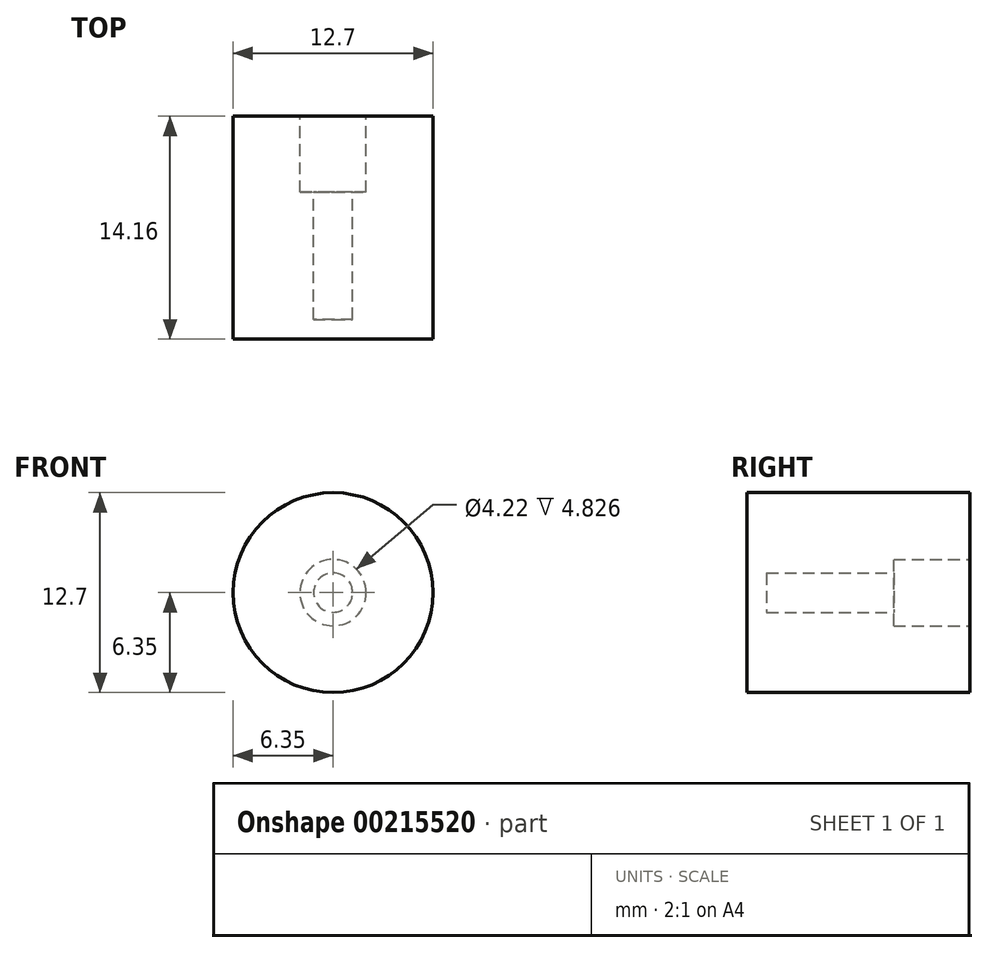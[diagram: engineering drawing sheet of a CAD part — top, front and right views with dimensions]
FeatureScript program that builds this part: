
annotation { "Feature Type Name" : "Feature", "Feature Type Description" : "" }
export const myFeature = defineFeature(function(context is Context, id is Id, definition is map)
    precondition{}
    {
        {
            var Q0;
            Q0=qCreatedBy(makeId("Front.planeOp"),FACE);
            var sketch = newSketch(context, id + "F0", { "sketchPlane" : qUnion([Q0])});
            skCircle(sketch, "E0", {"center": v(0, 0) * mm, "radius": 2.1 * mm});
            skCircle(sketch, "E1", {"center": v(0, 0) * mm, "radius": 6.35 * mm});
            skSolve(sketch);
        }
        {
            var Q0;
            Q0=makeQuery(id+"F0.imprint","IMPRINT",FACE,{"disambiguationData":[TD([[makeQuery(id+"F0.imprint","IMPRINT",EDGE,{"derivedFrom":sQuery(id+"F0.wireOp",EDGE,"E0")}),-1.0]])]});
            extrude(context, id + "F1", {"entities" : qUnion([Q0]), "depth" : 4.83 * mm});
        }
        {
            var Q0;
            Q0=makeQuery(id+"F1.opExtrude","CAP_FACE",FACE,{"disambiguationData":[OSD([sQuery(id+"F0.wireOp",EDGE,"E0"),sQuery(id+"F0.wireOp",EDGE,"E1")])],"isStart":false});
            var sketch = newSketch(context, id + "F2", { "sketchPlane" : qUnion([Q0])});
            skCircle(sketch, "E2", {"center": v(0, 0) * mm, "radius": 6.35 * mm});
            skSolve(sketch);
        }
        {
            var Q0;
            Q0=qSketchRegion(id+"F2",true);
            extrude(context, id + "F3", {"entities" : qUnion([Q0]), "operationType" : NewBodyOperationType.ADD, "depth" : 9.33 * mm});
        }
        {
            var Q0;
            Q0=makeQuery(id+"F3.opExtrude","CAP_FACE",FACE,{"disambiguationData":[OSD([sQuery(id+"F2.wireOp",EDGE,"E2")])],"isStart":true});
            var sketch = newSketch(context, id + "F4", { "sketchPlane" : qUnion([Q0])});
            skCircle(sketch, "E3", {"center": v(0, 0) * mm, "radius": 1.24 * mm});
            skSolve(sketch);
        }
        {
            var Q0;
            Q0 = qSketchRegion(id + "F4", true);
            extrude(context, id + "F5", {"entities" : qUnion([Q0]), "oppositeDirection" : true, "depth" : 8.08 * mm});
        }
    });
